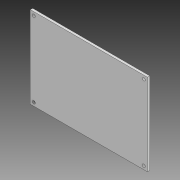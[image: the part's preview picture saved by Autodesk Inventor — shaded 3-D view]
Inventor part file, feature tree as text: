
AUTODESK INVENTOR PART (.ipt)
format: ipt  version: 2020 (Build 240168000, 168)  size: 88,064 bytes
history: native  units: mm
features: extrude x1, sketch x1
ambient origin geometry x8: Origin, YZ Plane, XZ Plane, XY Plane, X Axis, Y Axis, Z Axis, Center Point
bodies: Solid1 (feature_tree)
feature tree (2):
  extrude  "Extrusion1"  Depth=70.0mm
  sketch  "Sketch1"  dims[d0=100.0mm d1=70.0mm d2=2.0mm d3=0.0mm d4=64.0mm d5=94.0mm d6=2.5mm]
